# Revit family: AT-2_RFA
name_source: partatom
category: Plumbing Fixtures
units: mm (PartAtom-declared; Revit-internal decimal feet)

## family parameters
Always vertical = Yes
Cut with Voids When Loaded = No
OmniClass Number = 23.45.00.00
OmniClass Title = Sanitary, Laundry, and Cleaning Equipment
Part Type = Normal
Room Calculation Point = No
Round Connector Dimension = Use Diameter
Shared = Yes
Work Plane-Based = No

## types (1)
- AT-2
    Data Sheet = http://www.helvex.com.mx
    Default Elevation = 0"
    Description = Bearing Whit Standard Cap Seal
    Features = Premium Quality High Gloss; Antibacterial Protect; Adjustable Hinge
    Instructive = http://www.helvex.com.mx
    Manufacturer = HELVEX
    Model = AT-2
    Placement Height = 14.5"
    Polypropylene = Polypropylene
    Total Height = 2"
    Total Length = 19"
    Total Width = 14"
    Type Comments = SANIVEX
    URL = http://www.helvex.com.mx

## geometry (parser evidence)
native form markers: Sweep x3
no freeform markers — native parametric forms only
